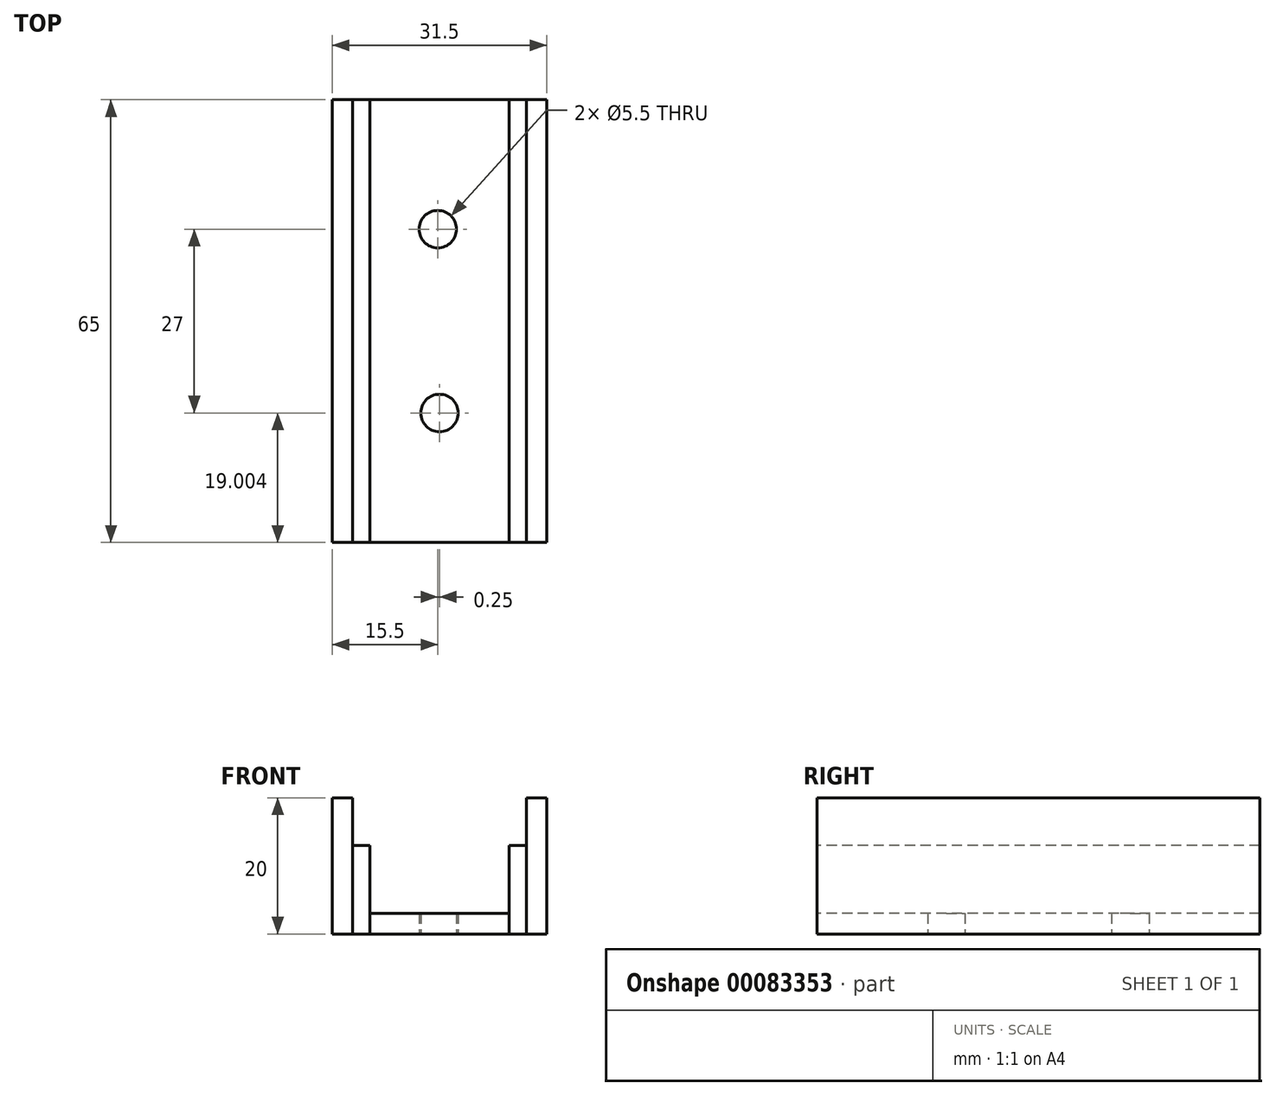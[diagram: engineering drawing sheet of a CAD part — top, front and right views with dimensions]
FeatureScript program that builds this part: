
annotation { "Feature Type Name" : "Feature", "Feature Type Description" : "" }
export const myFeature = defineFeature(function(context is Context, id is Id, definition is map)
    precondition{}
    {
        {
            var Q0;
            Q0=qCreatedBy(makeId("Top.planeOp"),FACE);
            var sketch = newSketch(context, id + "F0", { "sketchPlane" : qUnion([Q0])});
            skLineSegment(sketch, "E0.0", {"start": v(13, 8.45) * mm, "end": v(13, -56.55) * mm});
            skLineSegment(sketch, "E1.0", {"start": v(-12.5, -56.55) * mm, "end": v(-12.5, 8.45) * mm});
            skLineSegment(sketch, "E2", {"start": v(13, 8.45) * mm, "end": v(-12.5, 8.45) * mm});
            skLineSegment(sketch, "E3", {"start": v(13, -56.55) * mm, "end": v(-12.5, -56.55) * mm});
            skLineSegment(sketch, "E4.0", {"start": v(12.5, -10.55) * mm, "end": v(-12.5, -10.55) * mm, "construction": true});
            skPoint(sketch, "E5", {"position": v(0, -10.55) * mm});
            skLineSegment(sketch, "E6.0", {"start": v(-15.5, -56.55) * mm, "end": v(-15.5, 8.45) * mm});
            skLineSegment(sketch, "E7.0", {"start": v(16, 8.45) * mm, "end": v(16, -56.55) * mm});
            skLineSegment(sketch, "E8", {"start": v(16, 8.45) * mm, "end": v(13, 8.45) * mm});
            skLineSegment(sketch, "E9", {"start": v(-12.5, 8.45) * mm, "end": v(-15.5, 8.45) * mm});
            skLineSegment(sketch, "E10", {"start": v(-15.5, -56.55) * mm, "end": v(-12.5, -56.55) * mm});
            skLineSegment(sketch, "E11", {"start": v(16, -56.55) * mm, "end": v(13, -56.55) * mm});
            skLineSegment(sketch, "E12.0", {"start": v(-10, -56.55) * mm, "end": v(-10, 8.45) * mm});
            skLineSegment(sketch, "E13.0", {"start": v(10.5, 8.45) * mm, "end": v(10.5, -56.55) * mm});
            skLineSegment(sketch, "E14", {"start": v(-10, -37.55) * mm, "end": v(10.5, -37.55) * mm, "construction": true});
            skPoint(sketch, "E15", {"position": v(0.25, -37.55) * mm});
            skSolve(sketch);
        }
        {
            var Q0;
            {var subQ0=sQuery(id+"F0.wireOp",EDGE,"E12.0");Q0=makeQuery(id+"F0.imprint","IMPRINT",FACE,{"disambiguationData":[TD([[makeQuery(id+"F0.imprint","IMPRINT",EDGE,{"derivedFrom":subQ0}),-1.0]])]});}
            extrude(context, id + "F1", {"entities" : qUnion([Q0]), "depth" : 3 * mm});
        }
        {
            var Q0;
            Q0=makeQuery(id+"F0.imprint","IMPRINT",FACE,{"disambiguationData":[TD([[makeQuery(id+"F0.imprint","IMPRINT",EDGE,{"derivedFrom":sQuery(id+"F0.wireOp",EDGE,"E0.0")}),1.0]])]});
            var Q1;
            Q1=makeQuery(id+"F0.imprint","IMPRINT",FACE,{"disambiguationData":[TD([[makeQuery(id+"F0.imprint","IMPRINT",EDGE,{"derivedFrom":sQuery(id+"F0.wireOp",EDGE,"E1.0")}),1.0]])]});
            extrude(context, id + "F2", {"entities" : qUnion([Q0, Q1]), "operationType" : NewBodyOperationType.ADD, "depth" : 20 * mm});
        }
        {
            var Q0;
            Q0=sQuery(id+"F0.wireOp",VERTEX,"E5");
            var Q1;
            Q1=sQuery(id+"F0.wireOp",VERTEX,"E15");
            var Q2;
            Q2=makeQuery(id+"F1.opExtrude","SWEPT_BODY",BODY,{"disambiguationData":[OSD([sQuery(id+"F0.wireOp",EDGE,"E0.0"),sQuery(id+"F0.wireOp",EDGE,"E1.0"),sQuery(id+"F0.wireOp",EDGE,"E2"),sQuery(id+"F0.wireOp",EDGE,"E3")])]});
            hole(context, id + "F3", {"style" : HoleStyle.SIMPLE, "endStyle" : HoleEndStyle.THROUGH, "oppositeDirection" : true, "holeDiameter" : 5.5 * mm, "locations" : qUnion([Q0, Q1]), "scope" : qUnion([Q2]), "isTappedThrough" : true});
        }
        {
            var Q0;
            {var subQ0=sQuery(id+"F0.wireOp",EDGE,"E0.0");Q0=makeQuery(id+"F0.imprint","IMPRINT",FACE,{"disambiguationData":[TD([[makeQuery(id+"F0.imprint","IMPRINT",EDGE,{"derivedFrom":subQ0}),-1.0]])]});}
            var Q1;
            {var subQ0=sQuery(id+"F0.wireOp",EDGE,"E1.0");Q1=makeQuery(id+"F0.imprint","IMPRINT",FACE,{"disambiguationData":[TD([[makeQuery(id+"F0.imprint","IMPRINT",EDGE,{"derivedFrom":subQ0}),-1.0]])]});}
            extrude(context, id + "F4", {"entities" : qUnion([Q0, Q1]), "depth" : 13 * mm});
        }
    });
